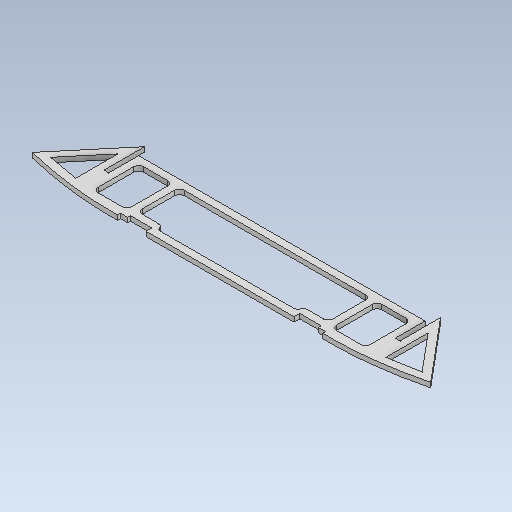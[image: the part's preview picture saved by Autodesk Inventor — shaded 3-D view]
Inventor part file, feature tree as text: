
AUTODESK INVENTOR PART (.ipt)
format: ipt  version: 2020.3 (Build 243373010, 373A)  size: 223,744 bytes
history: native  units: in
note: dims shown in document units (in); Inventor stores cm internally (conversion verified against a paired STEP export)
features: other x3, extrude x1, mirror x1, sketch x1
ambient origin geometry x8: Origin, YZ Plane, XZ Plane, XY Plane, X Axis, Y Axis, Z Axis, Center Point
bodies: Solid1 (feature_tree)
feature tree (6):
  other  "bulkhead_B2"
  other  "base_sketch.ipt"
  extrude  "Extrusion1"  Depth=0.1181in
  mirror  "Mirror1"
  other  "bulkhead_B2_plane"
  sketch  "Sketch2"  dims[d0=0.3937in d1=0.1181in d2=0.1181in d3=0.1181in d4=0.0787in d5=0.1181in d6=0.1181in d10=0.1181in d11=0.1181in d12=0.0787in d13=0.0787in d14=0.0in d15=0.1181in d16=0.1181in d17=0.7902in d18=0.0472in d19=0.0472in d20=0.2362in d22=0.2362in d23=0.1181in]
